# Revit family: PRE060001-FR
name_source: partatom
category: Appareils sanitaires
revit_build: Autodesk Revit 2017 (Build: 20160225_1515(x64)
units: mm (PartAtom-declared; Revit-internal decimal feet)

## family parameters
Basée sur le plan de construction = Non
Cote de connecteur circulaire = Utiliser le diamètre
Couper avec des vides une fois chargée = Non
Partagée = Non
Point de calcul de pièce = Non
Toujours verticalement = Oui
Type d'élément = Normal

## types (1)
- 71016 Presto Lavabo Mural Suspendu Evacuation invisible
    Adresse = 7, RUE RACINE - 92542 MONTROUGE CEDEX FRANCE
    Description = Lavabo Mural Suspendu Anti vandalisme 420x410mm
Partie basse fermée avec trappe d'accès et vis sécurités
Cuve Ø 320mm.
Fixation invisible, vidage perforé non amovible, siphon et grille de vidage G1"1/4. Utilisable par un utilisateur en fauteuil roulant.
Inox 304, Épaisseur 1/1,5mm, Finition Brossée
Marquage CE selon NF EN 14688
    Diamètre Nominal Sortie = 40 mm  [stored 0.131234 ft]
    Fabricant = LES ROBINETS PRESTO S.A.
    Finition = Inox AISI 304 (ISO Z7 CN 18.09)
    Flux Sortie = 0.1 L/s
    Fonction = Descriptif:
- Lavabo Mural Suspendu Anti vandalisme
- Fixation invisible
- Vidage perforé non amovible
- Trappe de maintenance sous le lavabo
- Utilisable par un utilisateur en fauteuil roulant

Matériaux:
- Inox AISI 304 (ISO Z7 CN 18.09)
- Épaisseur 1 et 1,5 mm
- Finition Brossée

Dimensions:
- Largeur 420mm
- Profondeur 410mm
- Hauteur 250mm
- Cuve Ø 320mm de diamètre et 145mm de profondeur
- Poids 5,2 kg

Livré avec:
- Siphon et grille de vidage G1"1/4 - Diamètre 40mm

Certification:
- Marquage CE
- Conforme à la norme EN 14688 - CL 00
    Garantie = 2
    H1 = 180 mm  [stored 0.590551 ft]
    Hauteur = 250 mm  [stored 0.82021 ft]
    L1 = 210 mm  [stored 0.688976 ft]
    Largeur = 420 mm  [stored 1.37795 ft]
    Lien CCTP = http://www.prestodatashare.com
    Lien fiche produit = http://www.prestodatashare.com
    Lien notice d'utilisation = http://www.prestodatashare.com
    Matériau = Inox
    Modèle = 71016 Presto Lavabo Mural Suspendu Evacuation invisible
    Perte de charge = 0.0 Pa
    Polantis code = PRE060001
    Profondeur = 410 mm  [stored 1.34514 ft]
    Reference = 71016
    URL = http://www.prestodatashare.com
    URL Fabricant = http://www.prestodatashare.com
    Variantes = 71016

note: [stored X ft] marks values corroborated as IEEE doubles in the binary element streams (Revit-internal decimal feet)
